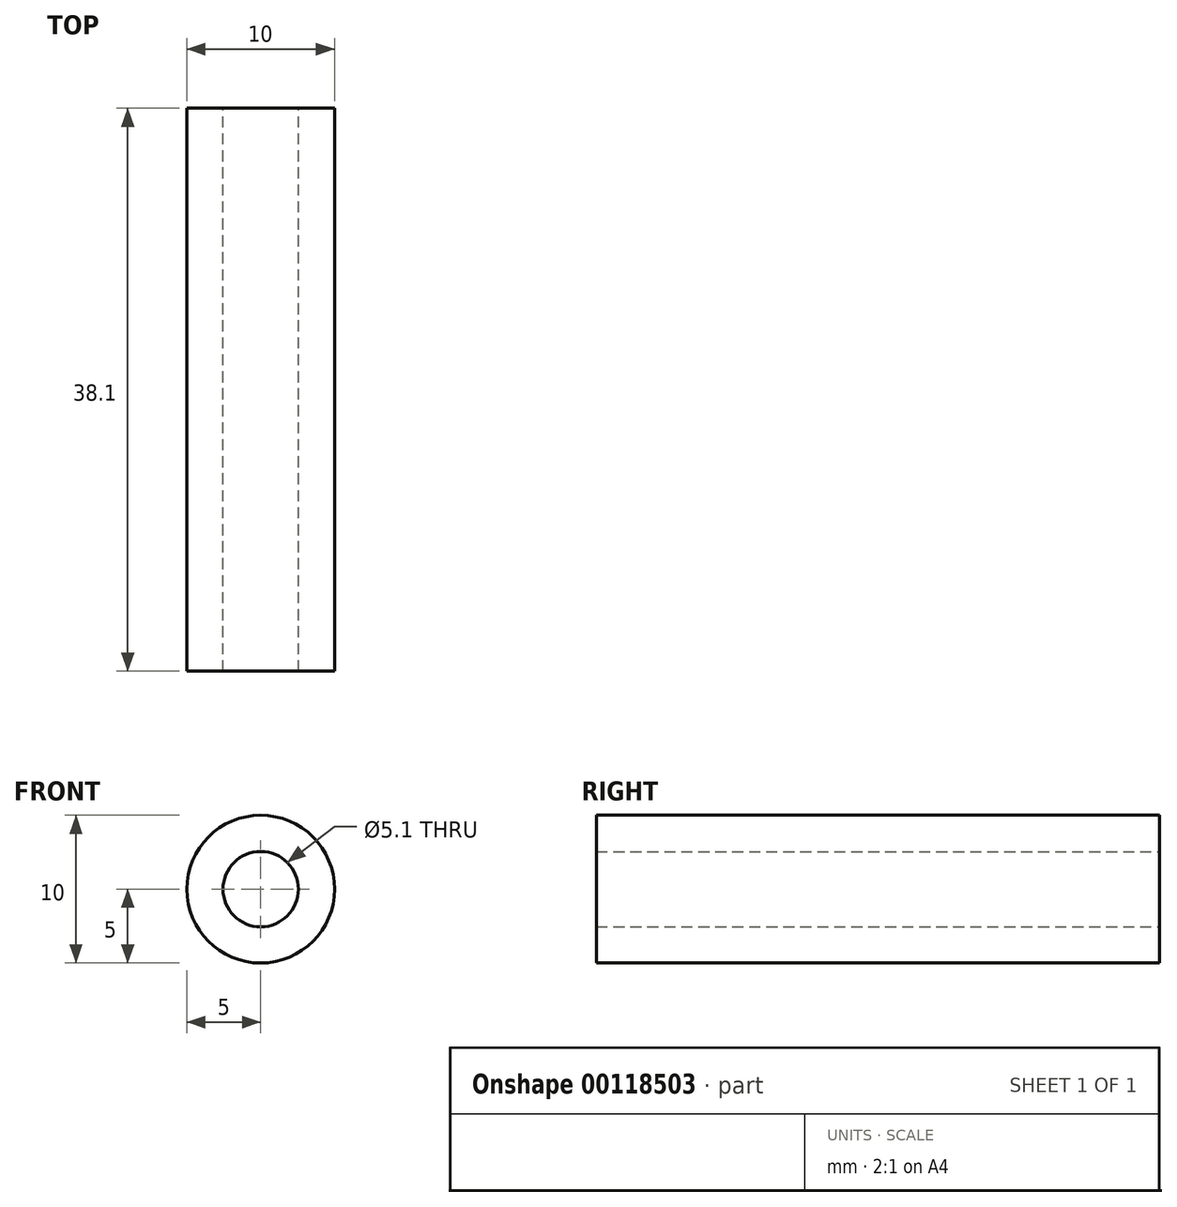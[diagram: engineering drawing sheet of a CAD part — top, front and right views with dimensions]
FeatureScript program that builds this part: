
annotation { "Feature Type Name" : "Feature", "Feature Type Description" : "" }
export const myFeature = defineFeature(function(context is Context, id is Id, definition is map)
    precondition{}
    {
        {
            var Q0;
            Q0=qCreatedBy(makeId("Front.planeOp"),FACE);
            var sketch = newSketch(context, id + "F0", { "sketchPlane" : qUnion([Q0])});
            skCircle(sketch, "E0", {"center": v(0, 0) * mm, "radius": 2.55 * mm});
            skCircle(sketch, "E1", {"center": v(0, 0) * mm, "radius": 5 * mm});
            skSolve(sketch);
        }
        {
            var Q0;
            Q0=makeQuery(id+"F0.imprint","IMPRINT",FACE,{"disambiguationData":[TD([[makeQuery(id+"F0.imprint","IMPRINT",EDGE,{"derivedFrom":sQuery(id+"F0.wireOp",EDGE,"E0")}),-1.0]])]});
            extrude(context, id + "F1", {"entities" : qUnion([Q0]), "depth" : 38.1 * mm, "symmetric" : true});
        }
    });
